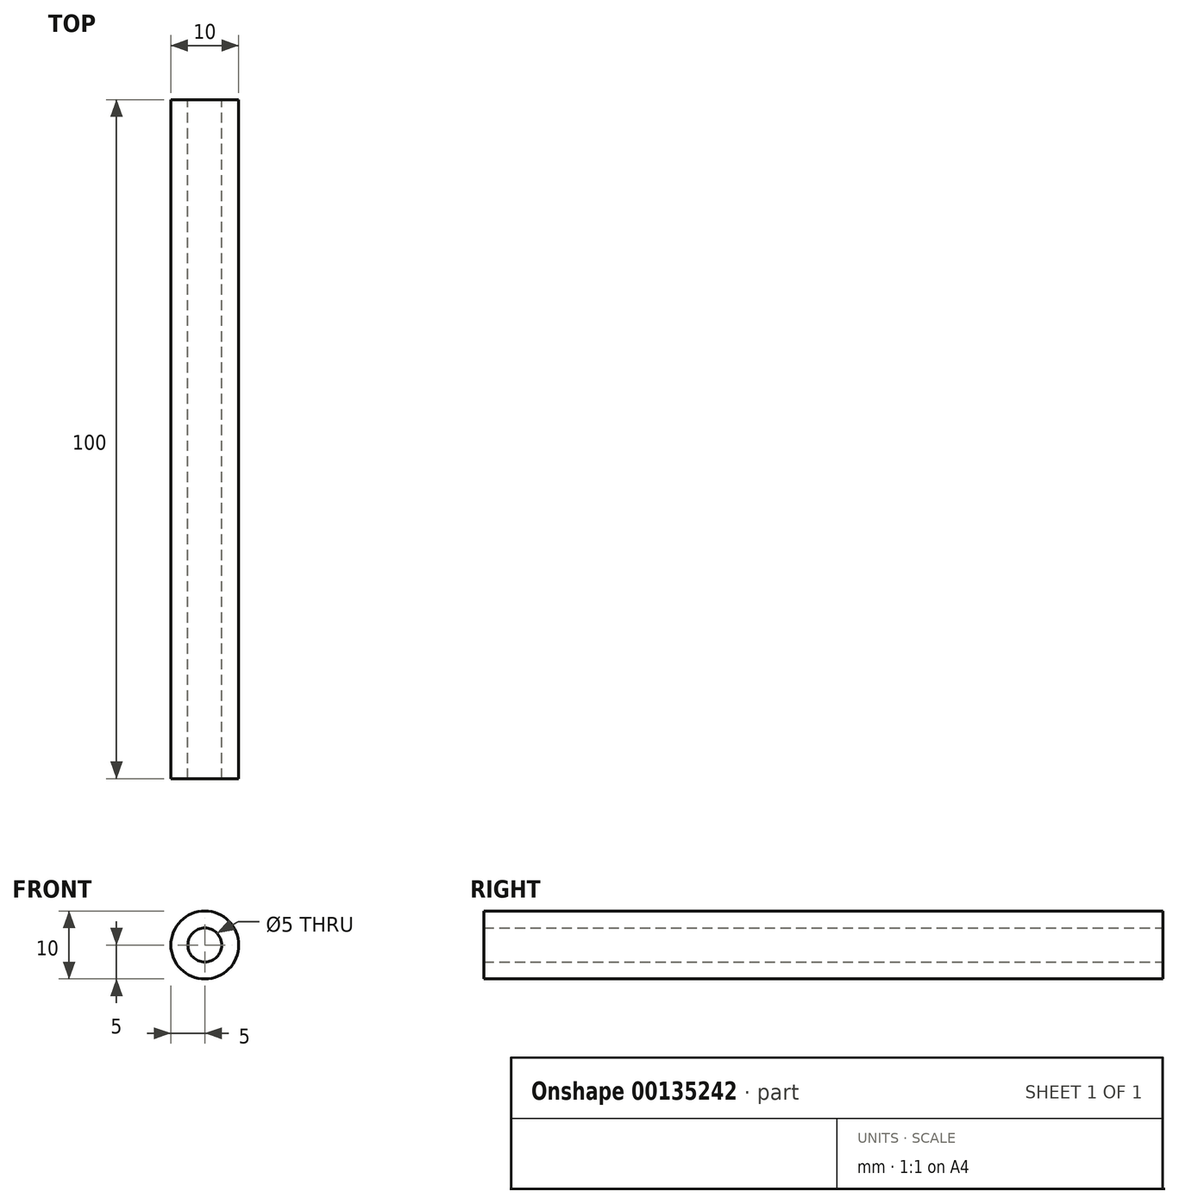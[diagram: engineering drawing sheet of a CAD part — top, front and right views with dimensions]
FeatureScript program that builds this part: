
annotation { "Feature Type Name" : "Feature", "Feature Type Description" : "" }
export const myFeature = defineFeature(function(context is Context, id is Id, definition is map)
    precondition{}
    {
        {
            var Q0;
            Q0=qCreatedBy(makeId("Front.planeOp"),FACE);
            var sketch = newSketch(context, id + "F0", { "sketchPlane" : qUnion([Q0])});
            skCircle(sketch, "E0", {"center": v(0, 0) * mm, "radius": 5 * mm});
            skCircle(sketch, "E1", {"center": v(0, 0) * mm, "radius": 2.5 * mm});
            skSolve(sketch);
        }
        {
            var Q0;
            Q0=makeQuery(id+"F0.imprint","IMPRINT",FACE,{"disambiguationData":[TD([[makeQuery(id+"F0.imprint","IMPRINT",EDGE,{"derivedFrom":sQuery(id+"F0.wireOp",EDGE,"E0")}),1.0]])]});
            extrude(context, id + "F1", {"entities" : qUnion([Q0]), "depth" : 100 * mm});
        }
    });
